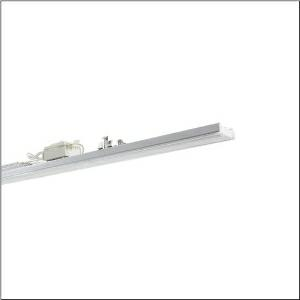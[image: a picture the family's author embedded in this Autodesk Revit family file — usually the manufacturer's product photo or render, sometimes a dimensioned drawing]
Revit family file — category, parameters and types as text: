
# Revit family: licross_21_recessed_mo_52tl11dn68xg3s
name_source: partatom
category: Lighting Fixtures
units: mm (PartAtom-declared; Revit-internal decimal feet)

## family parameters
Cut with Voids When Loaded = No
Host = Face
Light Source = No
Part Type = Normal
Room Calculation Point = No
Round Connector Dimension = Use Diameter
Shared = No

## types (1)
- --- (1 x LED, 910 lm, 6.7 W, 6500K)
    Apparent Load = 7 VA
    CIE Flux Codes = 89 96 99 100 100
    Color Rendering = 80
    Color Temperature = 6500K
    Default Elevation = 1800 mm
    Description = Licross 21 Recessed MO, luminaire insert, of sheet steel, galvanised, coil coated, white, length: 1.500mm, width: 66mm, height: 67mm, LED rated luminous flux: 8.000lm, light colour: 865, SDCM (Standard Deviation of Colour Matching)MacAdam ≤ 3 SDCM (initial), control gear: DALI 2 (for two DALI lines), with plug, 6-pole, with phase selection, for trunking rail, 14-core, mains connection: 220..240V, AC, 50/60Hz, rated input power: 46W, for emergency light function, internal wiring halogen-free, for trunking rail, 14-core, converter,control gear: single battery element, battery: LiFePO4, 9Ah, primary optical cover: cover, of PMMA, light emission: direct distribution, primary light characteristic: symmetric, protection rating (complete): IP40, insulation class (complete): insulation class I (protective earthing), certification: CE, UKCA, protection symbol: D if used in an environment without relevant dust loads with corresponding accessories, impact resistance: IK06, permissible ambient temperature for indoor applications: +5..+35°C, standard: EN 60598-2-22, corresponds to IFS (International Featured Standards) requirements for safety and quality in the food industry, reducing of maximum allowable ambient temperature of 5°C with ceiling mounting, LABS conformity tested according to VDMA 24364:2018-05, The light source and the operating device comply with the requirements of the Ecodesign Regulation (EU) 2019/2020 and are replaceable in accordance with this regulation, packaging unit: 1 piece
    Height = 58 mm
    Lamp = 1 x LED
    Lamp Light Flux = 910 lm
    Lamp Power = 6.7 W
    Lamp count = 1
    Length = 1500 mm
    Luminous efficacy = 136 lm/W
    Manufacturer = Siteco
    ModVariant = No
    Model = 52TL11DN68XG3S
    Mounting Place = Ceiling
    Mounting Type = Pendant
    Number of Poles = 1
    OnlyDefault = Yes
    Power Factor = 1
    Product Name = Licross 21 Recessed MO
    Product group = luminaire insert | ceiling pendant
    ProductGroupID = 901
    Protection Class = Protection class I
    Protection Degree = IP 40
    RLX_Detail_Level = 1
    RLX_Emergency_Light_Flux = 0 lm
    RLX_Emergency_Type = 0
    RLX_Emergency_Type_DB = No
    RlxData = <blob elided: 25269 chars, md5=730ea22c>
    Socket = socket
    Standby Power = 0 W
    System Light Flux = 910 lm
    System Power = 7 W
    Type Comments = : emergency light operation: 3 h
    Type Image = l_1296930.jpg
    URL = http://relux.com
    VarID = @adj_029983
    Voltage = 0 V
    Weight = 0.00 kg
    Width = 66 mm

## geometry (parser evidence)
native form markers: Blend x4, Sweep x11
no freeform markers — native parametric forms only
